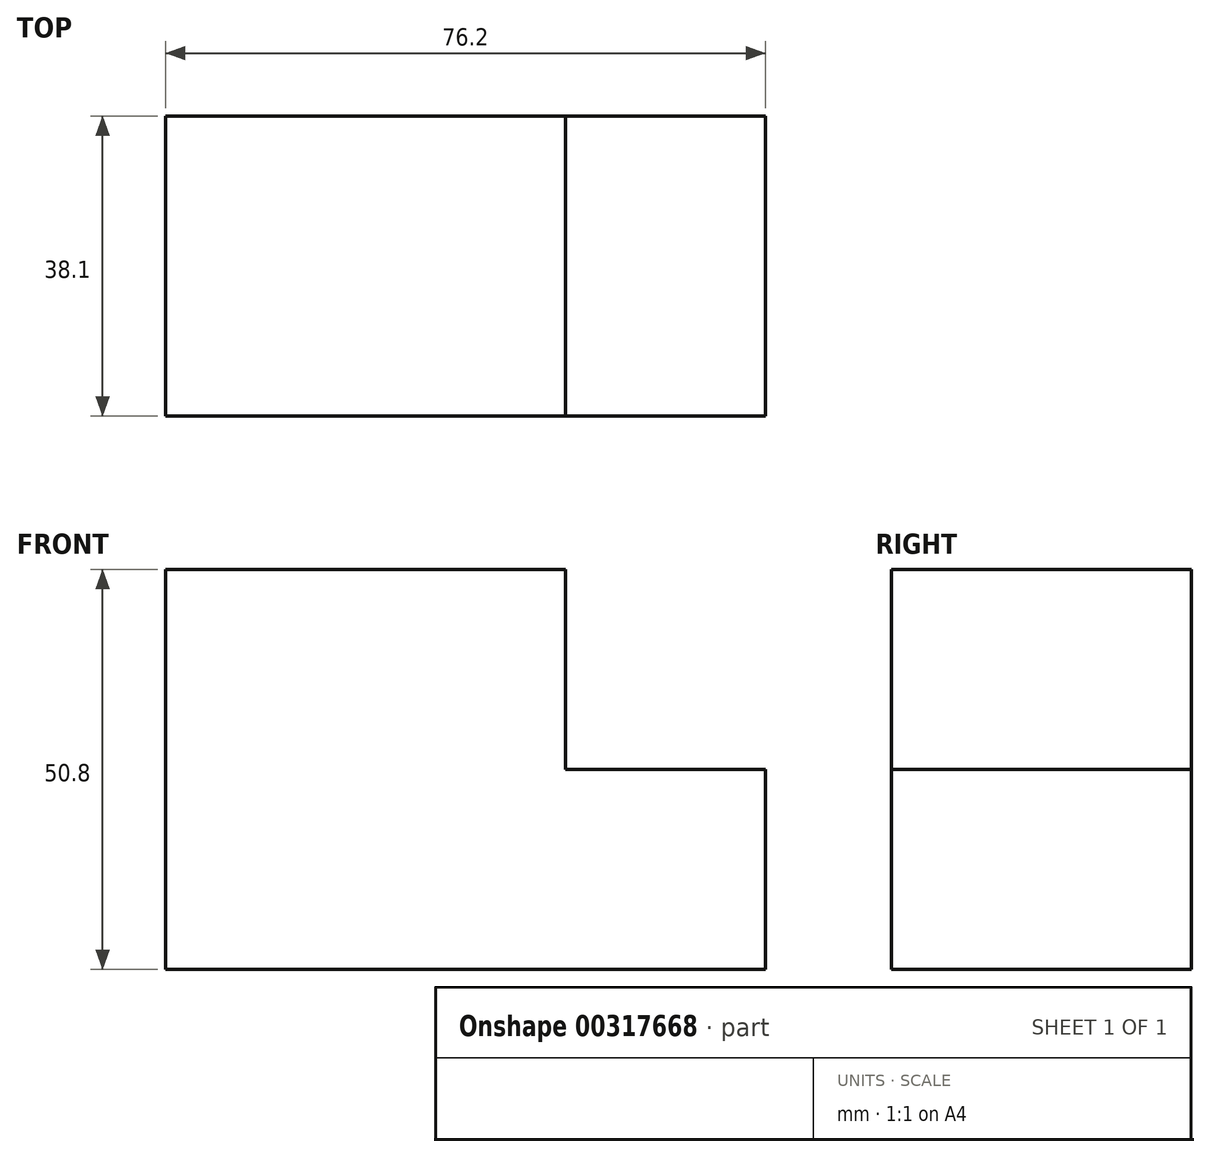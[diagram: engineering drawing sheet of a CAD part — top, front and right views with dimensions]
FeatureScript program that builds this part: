
annotation { "Feature Type Name" : "Feature", "Feature Type Description" : "" }
export const myFeature = defineFeature(function(context is Context, id is Id, definition is map)
    precondition{}
    {
        {
            var Q0;
            Q0=qCreatedBy(makeId("Front.planeOp"),FACE);
            var sketch = newSketch(context, id + "F0", { "sketchPlane" : qUnion([Q0])});
            skLineSegment(sketch, "E0", {"start": v(-73.02, 34.39) * mm, "end": v(-73.02, -16.41) * mm});
            skLineSegment(sketch, "E1", {"start": v(-73.02, -16.41) * mm, "end": v(3.18, -16.41) * mm});
            skLineSegment(sketch, "E2", {"start": v(3.18, -16.41) * mm, "end": v(3.18, 8.99) * mm});
            skLineSegment(sketch, "E3", {"start": v(3.18, 8.99) * mm, "end": v(-22.22, 8.99) * mm});
            skLineSegment(sketch, "E4", {"start": v(-22.22, 8.99) * mm, "end": v(-22.22, 34.39) * mm});
            skLineSegment(sketch, "E5", {"start": v(-22.22, 34.39) * mm, "end": v(-73.02, 34.39) * mm});
            skSolve(sketch);
        }
        {
            var Q0;
            Q0 = qSketchRegion(id + "F0", true);
            extrude(context, id + "F1", {"entities" : qUnion([Q0]), "depth" : 38.1 * mm});
        }
    });
